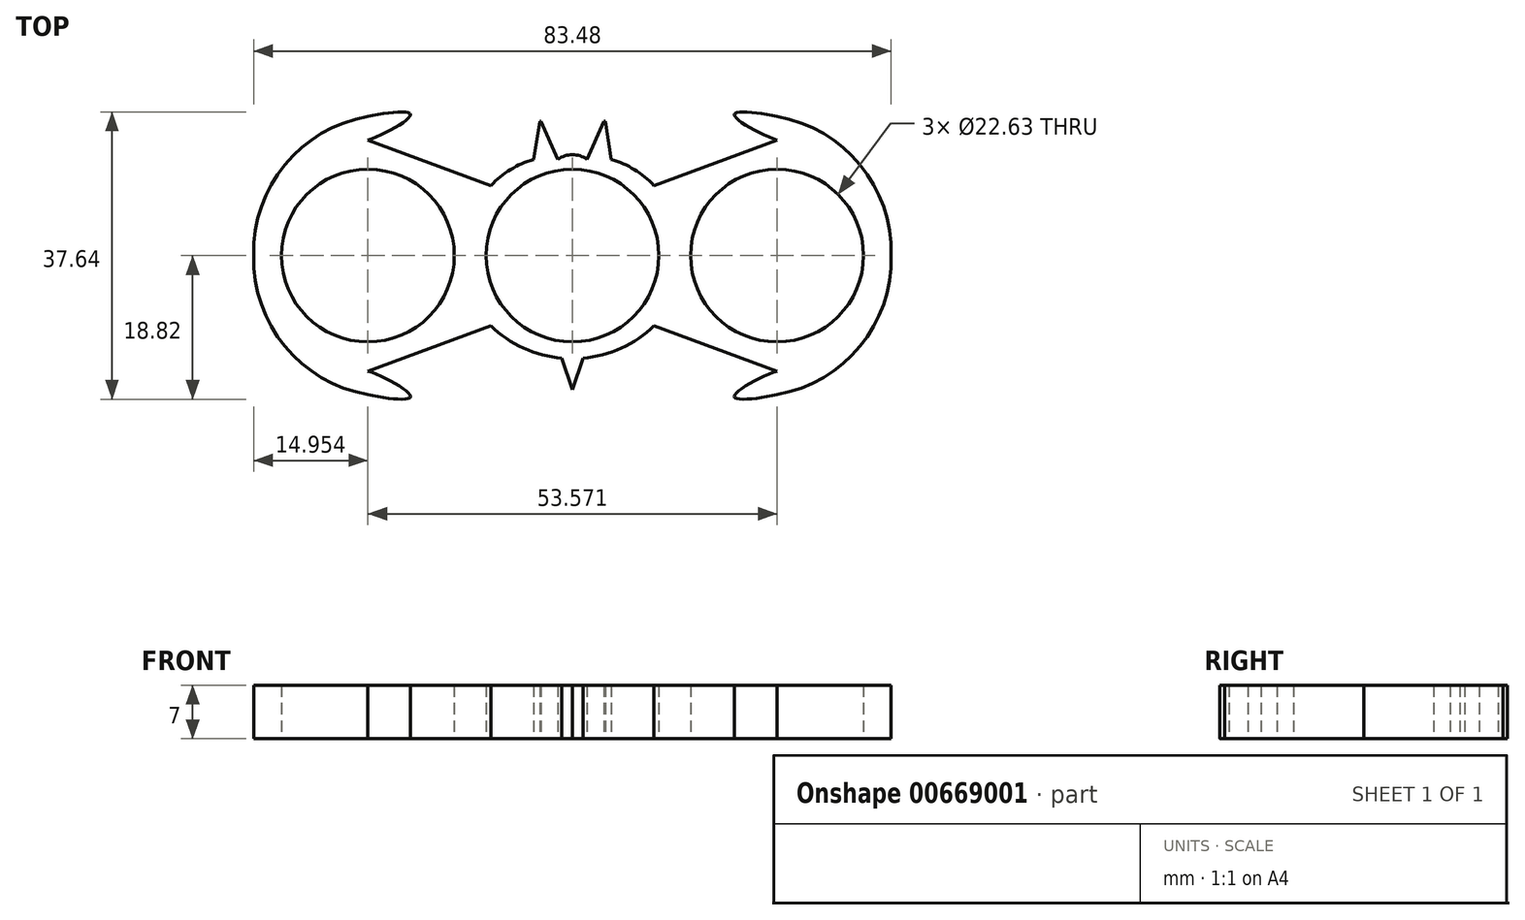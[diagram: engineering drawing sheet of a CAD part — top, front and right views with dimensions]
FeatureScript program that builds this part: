
annotation { "Feature Type Name" : "Feature", "Feature Type Description" : "" }
export const myFeature = defineFeature(function(context is Context, id is Id, definition is map)
    precondition{}
    {
        {
            var Q0;
            Q0=qCreatedBy(makeId("Top.planeOp"),FACE);
            var sketch = newSketch(context, id + "F0", { "sketchPlane" : qUnion([Q0])});
            skCircle(sketch, "E0", {"center": v(0, 0) * mm, "radius": 11.32 * mm});
            skCircle(sketch, "E1", {"center": v(0, 0) * mm, "radius": 45 * mm, "construction": true});
            skLineSegment(sketch, "E2", {"start": v(-5.1, 12.6) * mm, "end": v(-4.3, 17.6) * mm});
            skLineSegment(sketch, "E3", {"start": v(-4.3, 17.6) * mm, "end": v(-4.15, 17.6) * mm});
            skLineSegment(sketch, "E4", {"start": v(-4.15, 17.6) * mm, "end": v(-1.9, 12.6) * mm});
            skArc(sketch, "E5", {"start": v(-5.1, 12.6) * mm, "mid": v(-8.11, 11.26) * mm, "end": v(-10.68, 9.17) * mm});
            skArc(sketch, "E6.MirrorCS", {"start": v(5.1, 12.6) * mm, "mid": v(8.11, 11.26) * mm, "end": v(10.68, 9.17) * mm});
            skLineSegment(sketch, "E7.MirrorCS", {"start": v(5.1, 12.6) * mm, "end": v(4.3, 17.6) * mm});
            skLineSegment(sketch, "E8.MirrorCS", {"start": v(4.15, 17.6) * mm, "end": v(1.9, 12.6) * mm});
            skLineSegment(sketch, "E9.MirrorCS", {"start": v(4.3, 17.6) * mm, "end": v(4.15, 17.6) * mm});
            skArc(sketch, "E10", {"start": v(1.9, 12.6) * mm, "mid": v(0, 13.21) * mm, "end": v(-1.9, 12.6) * mm});
            skArc(sketch, "E11", {"start": v(-10.68, -9.17) * mm, "mid": v(-6.4, -12.14) * mm, "end": v(-1.38, -13.45) * mm});
            skLineSegment(sketch, "E12", {"start": v(-1.38, -13.45) * mm, "end": v(0, -17.6) * mm});
            skArc(sketch, "E13.MirrorCS", {"start": v(10.68, -9.17) * mm, "mid": v(6.4, -12.14) * mm, "end": v(1.38, -13.45) * mm});
            skLineSegment(sketch, "E14.MirrorCS", {"start": v(1.38, -13.45) * mm, "end": v(0, -17.6) * mm});
            skCircle(sketch, "E15", {"center": v(-26.79, 0) * mm, "radius": 11.32 * mm});
            skLineSegment(sketch, "E16", {"start": v(-26.79, 0) * mm, "end": v(-26.79, 26.28) * mm, "construction": true});
            skLineSegment(sketch, "E17", {"start": v(-26.79, 0) * mm, "end": v(-26.79, -29.82) * mm, "construction": true});
            skLineSegment(sketch, "E18", {"start": v(-10.68, 9.17) * mm, "end": v(-26.79, 15.14) * mm});
            skLineSegment(sketch, "E19.MirrorCS", {"start": v(-10.68, -9.17) * mm, "end": v(-26.79, -15.14) * mm});
            skArc(sketch, "E20", {"start": v(-26.79, 18.22) * mm, "mid": v(-37.65, 11.89) * mm, "end": v(-41.73, 0) * mm});
            skArc(sketch, "E21.MirrorCS", {"start": v(-26.79, -18.22) * mm, "mid": v(-37.65, -11.89) * mm, "end": v(-41.73, 0) * mm});
            skFitSpline(sketch, "E22", {"points": [v(-26.79, 18.22) * mm, v(-21.2, 18.46) * mm, v(-26.79, 15.14) * mm], "startDerivative": vector(14.49, 3.26) * mm, "endDerivative": vector(-11.35, -3.52) * mm});
            skFitSpline(sketch, "E23.MirrorCS", {"points": [v(-26.79, -18.22) * mm, v(-21.2, -18.46) * mm, v(-26.79, -15.14) * mm], "startDerivative": vector(14.49, -3.26) * mm, "endDerivative": vector(-11.35, 3.52) * mm});
            skLineSegment(sketch, "E24.MirrorCS", {"start": v(10.68, 9.17) * mm, "end": v(26.79, 15.14) * mm});
            skFitSpline(sketch, "E25.MirrorCS", {"points": [v(26.79, 18.22) * mm, v(21.2, 18.46) * mm, v(26.79, 15.14) * mm], "startDerivative": vector(-14.49, 3.26) * mm, "endDerivative": vector(11.35, -3.52) * mm});
            skArc(sketch, "E26.MirrorCS", {"start": v(26.79, 18.22) * mm, "mid": v(37.65, 11.89) * mm, "end": v(41.73, 0) * mm});
            skArc(sketch, "E27.MirrorCS", {"start": v(26.79, -18.22) * mm, "mid": v(37.65, -11.89) * mm, "end": v(41.73, 0) * mm});
            skFitSpline(sketch, "E28.MirrorCS", {"points": [v(26.79, -18.22) * mm, v(21.2, -18.46) * mm, v(26.79, -15.14) * mm], "startDerivative": vector(-14.49, -3.26) * mm, "endDerivative": vector(11.35, 3.52) * mm});
            skLineSegment(sketch, "E29.MirrorCS", {"start": v(10.68, -9.17) * mm, "end": v(26.79, -15.14) * mm});
            skCircle(sketch, "E30.MirrorC", {"center": v(26.79, 0) * mm, "radius": 11.32 * mm});
            skSolve(sketch);
        }
        {
            var Q0;
            Q0 = qSketchRegion(id + "F0", true);
            extrude(context, id + "F1", {"entities" : qUnion([Q0]), "depth" : 7 * mm, "offsetDistance" : 25 * mm});
        }
    });
